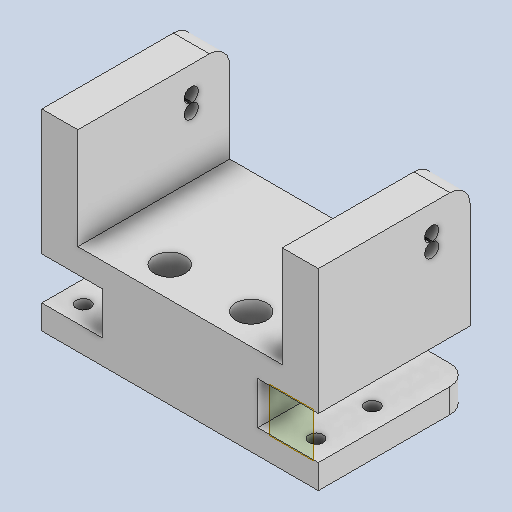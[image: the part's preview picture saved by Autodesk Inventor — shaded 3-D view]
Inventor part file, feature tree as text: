
AUTODESK INVENTOR PART (.ipt)
format: ipt  version: 2022 (Build 260153000, 153)  size: 211,456 bytes
history: native  units: in
note: dims shown in document units (in); Inventor stores cm internally (conversion verified against a paired STEP export)
features: reference x7, extrude x5, sketch x5, other x5, plane x1, fillet x1, mirror x1, projected_geometry x1
ambient origin geometry x8: Origin, YZ Plane, XZ Plane, XY Plane, X Axis, Y Axis, Z Axis, Center Point
bodies: Solid1 (feature_tree)
feature tree (26):
  plane  "Work Plane1"
  extrude  "Extrusion1"  TaperAngle=0.0deg  [1 undecoded]
  extrude  "Extrusion2"  Depth=0.1969in
  extrude  "Extrusion3"  Depth=0.7874in
  fillet  "Fillet1"  Radius=0.7874in
  mirror  "Mirror1"
  extrude  "Extrusion4"  Depth=1.1811in TaperAngle=0.0deg
  extrude  "Extrusion5"  Depth=1.1811in TaperAngle=0.0deg
  sketch  "Sketch1"  dims[d0=0.1969in d1=0.0in]
  reference  "Reference1"
  reference  "Reference2"
  reference  "Reference3"
  sketch  "Sketch2"  dims[d2=0.0079in d3=0.1969in]
  reference  "Reference4"
  sketch  "Sketch3"  dims[d4=0.0079in d5=0.0079in d6=0.7874in]
  reference  "Reference5"
  sketch  "Sketch4"  dims[d7=0.0079in d8=1.1811in d9=0.0in]
  projected_geometry  "Projected Loop1"
  reference  "Reference6"
  sketch  "Skizze5"  dims[d10=0.2402in d11=1.0in d12=0.0in d13=0.2362in d14=1.1811in d15=0.0in d16=0.1575in d17=0.1102in d18=0.1102in d19=0.1102in d20=0.1102in d21=0.1703in d22=0.1703in d23=0.1703in d24=1.1811in d25=0.0in d26=0.1102in d27=0.0in d28=0.0in]
  reference  "Referenz7"
  other  "Assembly_Lightsheet_Focus.iam"
  other  "30_XY_Sample_lightsheetarm_v3:1"
  other  "00_rod_6mm:2"
  other  "<userpath>\Dropbox\UC2\02_CAD\INVENTOR\uc2_v3\Assembly_Lightsheet_Focus.iam"
  other  "30_Cube_Z_Focus_MGN12_manual_gear_v3:1"
note: 1 required parameter value undecoded (feature->parameter linkage not recoverable at this tier; creation-order binding heuristic only, values carry confidence <= 0.55)
